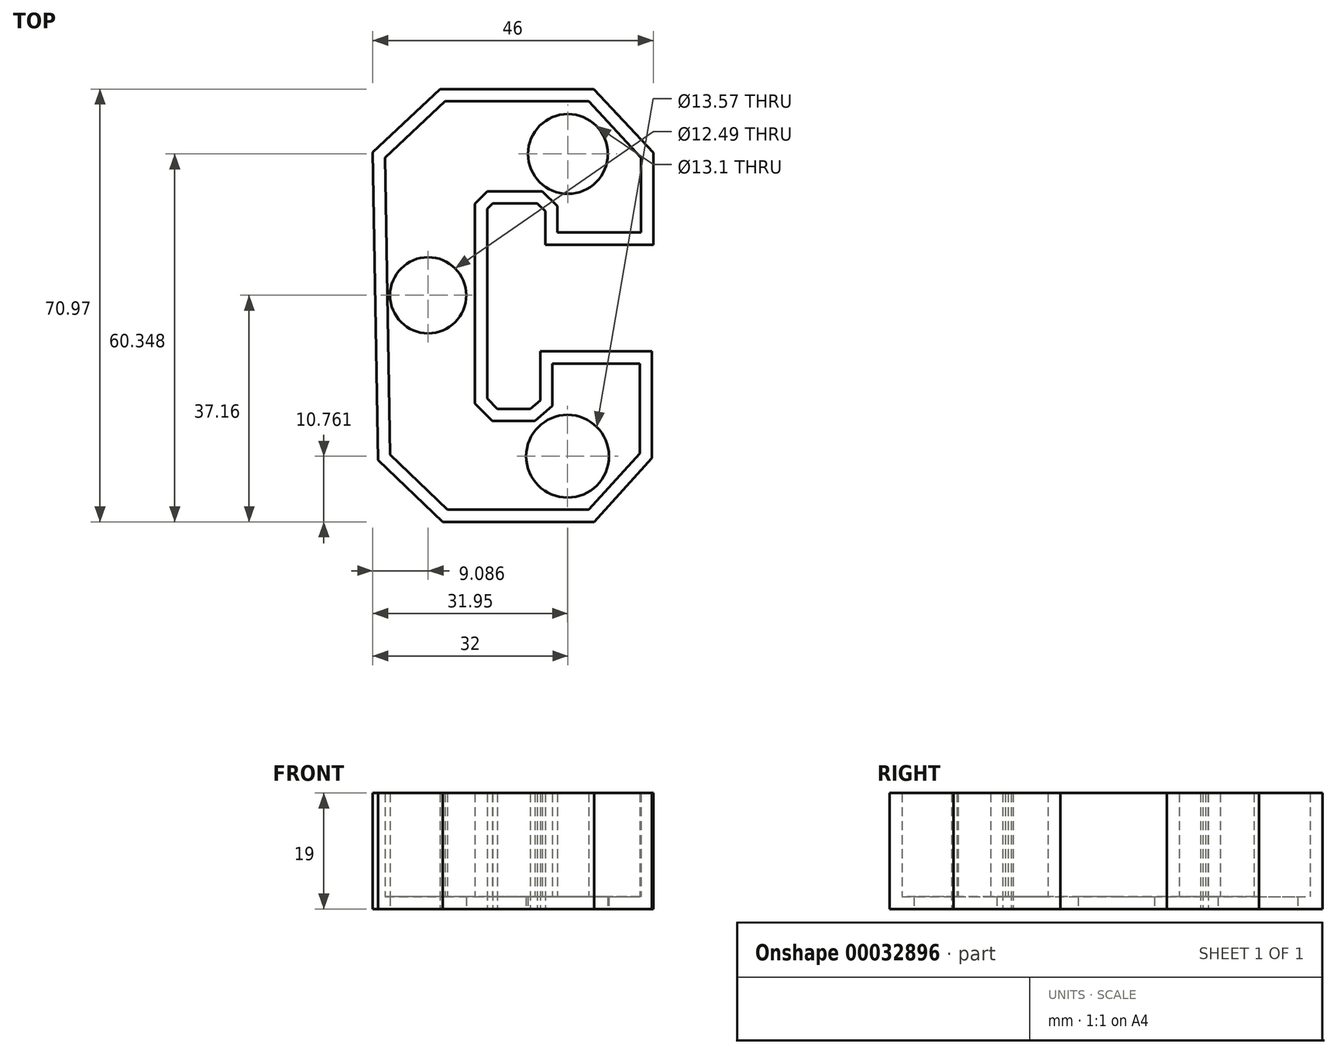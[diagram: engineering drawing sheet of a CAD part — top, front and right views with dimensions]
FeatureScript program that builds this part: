
annotation { "Feature Type Name" : "Feature", "Feature Type Description" : "" }
export const myFeature = defineFeature(function(context is Context, id is Id, definition is map)
    precondition{}
    {
        {
            var Q0;
            Q0=qCreatedBy(makeId("Top.planeOp"),FACE);
            var sketch = newSketch(context, id + "F0", { "sketchPlane" : qUnion([Q0])});
            skLineSegment(sketch, "E0", {"start": v(-33.38, 26.93) * mm, "end": v(-23.55, 36.15) * mm});
            skLineSegment(sketch, "E1", {"start": v(-23.55, 36.15) * mm, "end": v(0, 36.15) * mm});
            skLineSegment(sketch, "E2", {"start": v(0, 36.15) * mm, "end": v(8.6, 26.93) * mm});
            skLineSegment(sketch, "E3", {"start": v(8.6, 26.93) * mm, "end": v(8.6, 14.64) * mm});
            skLineSegment(sketch, "E4", {"start": v(8.6, 14.64) * mm, "end": v(-5.12, 14.64) * mm});
            skLineSegment(sketch, "E5", {"start": v(-5.12, 14.64) * mm, "end": v(-5.12, 18.95) * mm});
            skLineSegment(sketch, "E6", {"start": v(-5.12, 18.95) * mm, "end": v(-7.58, 21.4) * mm});
            skLineSegment(sketch, "E7", {"start": v(-7.58, 21.4) * mm, "end": v(-16.59, 21.4) * mm});
            skLineSegment(sketch, "E8", {"start": v(-16.59, 21.4) * mm, "end": v(-18.64, 19.35) * mm});
            skLineSegment(sketch, "E9", {"start": v(-18.64, 19.35) * mm, "end": v(-18.64, -13.42) * mm});
            skLineSegment(sketch, "E10", {"start": v(-18.64, -13.42) * mm, "end": v(-15.77, -16.28) * mm});
            skLineSegment(sketch, "E11", {"start": v(-15.77, -16.28) * mm, "end": v(-8.8, -16.28) * mm});
            skLineSegment(sketch, "E12", {"start": v(-8.8, -16.28) * mm, "end": v(-5.94, -13.82) * mm});
            skLineSegment(sketch, "E13", {"start": v(-5.94, -13.82) * mm, "end": v(-5.94, -6.86) * mm});
            skLineSegment(sketch, "E14", {"start": v(-5.94, -6.86) * mm, "end": v(8.4, -6.86) * mm});
            skLineSegment(sketch, "E15", {"start": v(8.4, -6.86) * mm, "end": v(8.4, -21.6) * mm});
            skLineSegment(sketch, "E16", {"start": v(8.4, -21.6) * mm, "end": v(0, -30.82) * mm});
            skLineSegment(sketch, "E17", {"start": v(0, -30.82) * mm, "end": v(-23.14, -30.82) * mm});
            skLineSegment(sketch, "E18", {"start": v(-23.14, -30.82) * mm, "end": v(-32.57, -21.81) * mm});
            skLineSegment(sketch, "E19", {"start": v(-32.57, -21.81) * mm, "end": v(-33.38, 26.93) * mm});
            skSolve(sketch);
        }
        {
            var Q0;
            Q0=makeQuery(id+"F0.imprint","IMPRINT",FACE,{"disambiguationData":[TD([[makeQuery(id+"F0.imprint","IMPRINT",EDGE,{"derivedFrom":sQuery(id+"F0.wireOp",EDGE,"E0")}),-1.0]])]});
            extrude(context, id + "F1", {"entities" : qUnion([Q0]), "depth" : 17 * mm});
        }
        {
            var Q0;
            Q0=makeQuery(id+"F1.opExtrude","CAP_FACE",FACE,{"disambiguationData":[OSD([sQuery(id+"F0.wireOp",EDGE,"E0"),sQuery(id+"F0.wireOp",EDGE,"E1"),sQuery(id+"F0.wireOp",EDGE,"E2"),sQuery(id+"F0.wireOp",EDGE,"E3"),sQuery(id+"F0.wireOp",EDGE,"E4"),sQuery(id+"F0.wireOp",EDGE,"E5"),sQuery(id+"F0.wireOp",EDGE,"E6"),sQuery(id+"F0.wireOp",EDGE,"E7"),sQuery(id+"F0.wireOp",EDGE,"E8"),sQuery(id+"F0.wireOp",EDGE,"E9"),sQuery(id+"F0.wireOp",EDGE,"E10"),sQuery(id+"F0.wireOp",EDGE,"E11"),sQuery(id+"F0.wireOp",EDGE,"E12"),sQuery(id+"F0.wireOp",EDGE,"E13"),sQuery(id+"F0.wireOp",EDGE,"E14"),sQuery(id+"F0.wireOp",EDGE,"E15"),sQuery(id+"F0.wireOp",EDGE,"E16"),sQuery(id+"F0.wireOp",EDGE,"E17"),sQuery(id+"F0.wireOp",EDGE,"E18"),sQuery(id+"F0.wireOp",EDGE,"E19")])],"isStart":false});
            shell(context, id + "F2", {"entities" : qUnion([Q0]), "thickness" : 2 * mm, "oppositeDirection" : true});
        }
        {
            var Q0;
            Q0=makeQuery(id+"F1.opExtrude","CAP_FACE",FACE,{"disambiguationData":[OSD([sQuery(id+"F0.wireOp",EDGE,"E0"),sQuery(id+"F0.wireOp",EDGE,"E1"),sQuery(id+"F0.wireOp",EDGE,"E2"),sQuery(id+"F0.wireOp",EDGE,"E3"),sQuery(id+"F0.wireOp",EDGE,"E4"),sQuery(id+"F0.wireOp",EDGE,"E5"),sQuery(id+"F0.wireOp",EDGE,"E6"),sQuery(id+"F0.wireOp",EDGE,"E7"),sQuery(id+"F0.wireOp",EDGE,"E8"),sQuery(id+"F0.wireOp",EDGE,"E9"),sQuery(id+"F0.wireOp",EDGE,"E10"),sQuery(id+"F0.wireOp",EDGE,"E11"),sQuery(id+"F0.wireOp",EDGE,"E12"),sQuery(id+"F0.wireOp",EDGE,"E13"),sQuery(id+"F0.wireOp",EDGE,"E14"),sQuery(id+"F0.wireOp",EDGE,"E15"),sQuery(id+"F0.wireOp",EDGE,"E16"),sQuery(id+"F0.wireOp",EDGE,"E17"),sQuery(id+"F0.wireOp",EDGE,"E18"),sQuery(id+"F0.wireOp",EDGE,"E19")])],"isStart":true});
            var sketch = newSketch(context, id + "F3", { "sketchPlane" : qUnion([Q0])});
            skCircle(sketch, "E20", {"center": v(-3.4, -27.53) * mm, "radius": 6.55 * mm});
            skCircle(sketch, "E21", {"center": v(-26.31, -4.34) * mm, "radius": 6.25 * mm});
            skCircle(sketch, "E22", {"center": v(-3.45, 22.06) * mm, "radius": 6.79 * mm});
            skSolve(sketch);
        }
        {
            var Q0;
            Q0=makeQuery(id+"F3.imprint","IMPRINT",FACE,{"disambiguationData":[TD([[makeQuery(id+"F3.imprint","IMPRINT",EDGE,{"derivedFrom":sQuery(id+"F3.wireOp",EDGE,"E20")}),1.0]])]});
            var Q1;
            Q1=makeQuery(id+"F3.imprint","IMPRINT",FACE,{"disambiguationData":[TD([[makeQuery(id+"F3.imprint","IMPRINT",EDGE,{"derivedFrom":sQuery(id+"F3.wireOp",EDGE,"E21")}),1.0]])]});
            var Q2;
            Q2=makeQuery(id+"F3.imprint","IMPRINT",FACE,{"disambiguationData":[TD([[makeQuery(id+"F3.imprint","IMPRINT",EDGE,{"derivedFrom":sQuery(id+"F3.wireOp",EDGE,"E22")}),1.0]])]});
            extrude(context, id + "F4", {"entities" : qUnion([Q0, Q1, Q2]), "operationType" : NewBodyOperationType.REMOVE, "oppositeDirection" : true, "depth" : 30 * mm});
        }
    });
